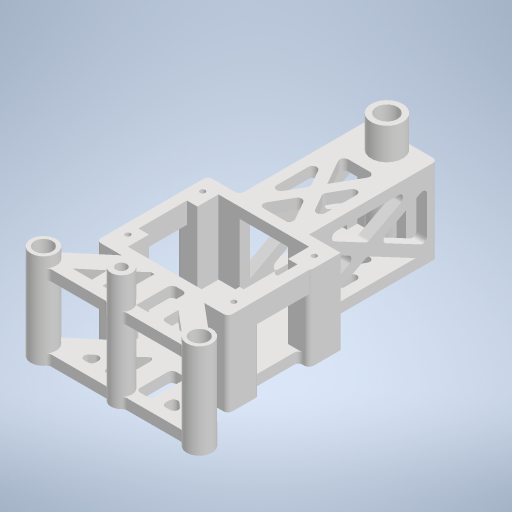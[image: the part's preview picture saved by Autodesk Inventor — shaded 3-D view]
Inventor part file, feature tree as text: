
AUTODESK INVENTOR PART (.ipt)
format: ipt  version: 2023 (Build 270158000, 158)  size: 1,316,864 bytes
history: native  units: mm
features: projected_geometry x33, extrude x15, sketch x11, fillet x3
ambient origin geometry x8: Origin, YZ Plane, XZ Plane, XY Plane, X Axis, Y Axis, Z Axis, Center Point
bodies: Body1 (feature_tree)
feature tree (62):
  sketch  "Sketch1"  dims[d0=43.0mm d1=43.0mm]
  extrude  "Extrusion5"  Depth=43.0mm
  extrude  "Extrusion6"  Depth=53.0mm
  extrude  "Extrusion7"  Depth=10.0mm
  extrude  "Extrusion11"  Depth=5.0mm
  extrude  "Extrusion12"  Depth=53.0mm
  extrude  "Extrusion13"  Depth=5.0mm
  extrude  "Extrusion14"  Depth=10.0mm
  extrude  "Extrusion15"  Depth=15.0mm
  extrude  "Extrusion16"  Depth=35.0mm TaperAngle=0.0deg
  extrude  "Extrusion17"  Depth=10.0mm
  extrude  "Extrusion18"  Depth=10.0mm
  extrude  "Extrusion19"  Depth=15.0mm
  extrude  "Extrusion20"  Depth=2.5mm
  extrude  "Extrusion21"  Depth=2.5mm
  fillet  "Fillet3"  Radius=2.5mm
  fillet  "Fillet4"  Radius=2.5mm
  fillet  "Fillet5"  Radius=15.0mm
  extrude  "Extrusion22"  Depth=0.5mm
  sketch  "Sketch2"  dims[d2=53.0mm d3=53.0mm]
  projected_geometry  "Projected Loop1"
  projected_geometry  "Projected Loop2"
  projected_geometry  "Projected Loop3"
  projected_geometry  "Projected Loop4"
  sketch  "Sketch8"  dims[d4=15.0mm d5=10.0mm]
  projected_geometry  "Projected Loop10"
  projected_geometry  "Projected Loop11"
  projected_geometry  "Projected Loop12"
  projected_geometry  "Projected Loop13"
  sketch  "Sketch10"  dims[d7=5.0mm d8=27.0mm]
  projected_geometry  "Projected Loop14"
  projected_geometry  "Projected Loop15"
  sketch  "Sketch11"  dims[d9=10.0mm d10=53.0mm]
  projected_geometry  "Projected Loop16"
  projected_geometry  "Projected Loop17"
  projected_geometry  "Projected Loop18"
  projected_geometry  "Projected Loop19"
  projected_geometry  "Projected Loop20"
  sketch  "Sketch12"  dims[d11=53.0mm d12=5.0mm]
  sketch  "Sketch13"  dims[d13=27.0mm d23=10.0mm]
  projected_geometry  "Projected Loop21"
  projected_geometry  "Projected Loop22"
  projected_geometry  "Projected Loop23"
  sketch  "Sketch14"  dims[d25=15.0mm d28=77.457754mm]
  projected_geometry  "Projected Loop24"
  projected_geometry  "Projected Loop25"
  projected_geometry  "Projected Loop26"
  projected_geometry  "Projected Loop27"
  projected_geometry  "Projected Loop28"
  sketch  "Sketch16"  dims[d29=5.0mm d30=0.0mm d31=35.0mm d32=0.0mm]
  projected_geometry  "Projected Loop29"
  projected_geometry  "Projected Loop30"
  projected_geometry  "Projected Loop31"
  sketch  "Sketch18"  dims[d34=5.0mm d35=10.0mm]
  projected_geometry  "Projected Loop34"
  projected_geometry  "Projected Loop35"
  projected_geometry  "Projected Loop36"
  projected_geometry  "Projected Loop37"
  projected_geometry  "Projected Loop38"
  projected_geometry  "Projected Loop39"
  sketch  "Sketch20"  dims[d37=15.0mm d38=10.0mm d39=15.0mm d40=2.5mm d41=2.5mm d42=2.5mm d43=2.5mm d44=15.0mm d45=0.0mm d60=48.849mm d61=5.0mm d62=50.0mm d63=10.0mm d64=74.0mm d65=8.0mm d66=12.0mm d68=8.0mm d69=5.0mm d70=35.0mm d71=0.0mm d72=5.0mm d73=0.0mm d74=17.103mm d75=10.0mm d76=5.0mm d77=0.0mm d78=0.0mm d81=8.5mm d83=5.0mm d84=2.5mm d85=2.5mm d86=2.5mm d87=2.5mm d88=5.0mm d89=0.0mm d95=5.0mm d96=0.0mm d97=5.0mm d98=5.0mm d99=10.0mm d100=0.0mm d101=5.0mm d102=5.0mm d103=5.0mm d104=0.0mm d105=2.0mm d106=0.0mm d107=5.0mm d108=0.0mm d109=5.0mm d110=10.0mm d111=25.0mm d112=0.0mm d113=5.0mm d114=10.0mm d115=25.0mm d116=0.0mm d117=2.0mm d118=2.0mm d119=2.0mm d121=8.5mm d122=8.5mm d123=5.0mm d124=0.0mm d22=0.5mm d24=0.5mm d55=0.5mm d56=0.872665mm d57=0.5mm d58=0.872665mm]
  projected_geometry  "Projected Loop40"
